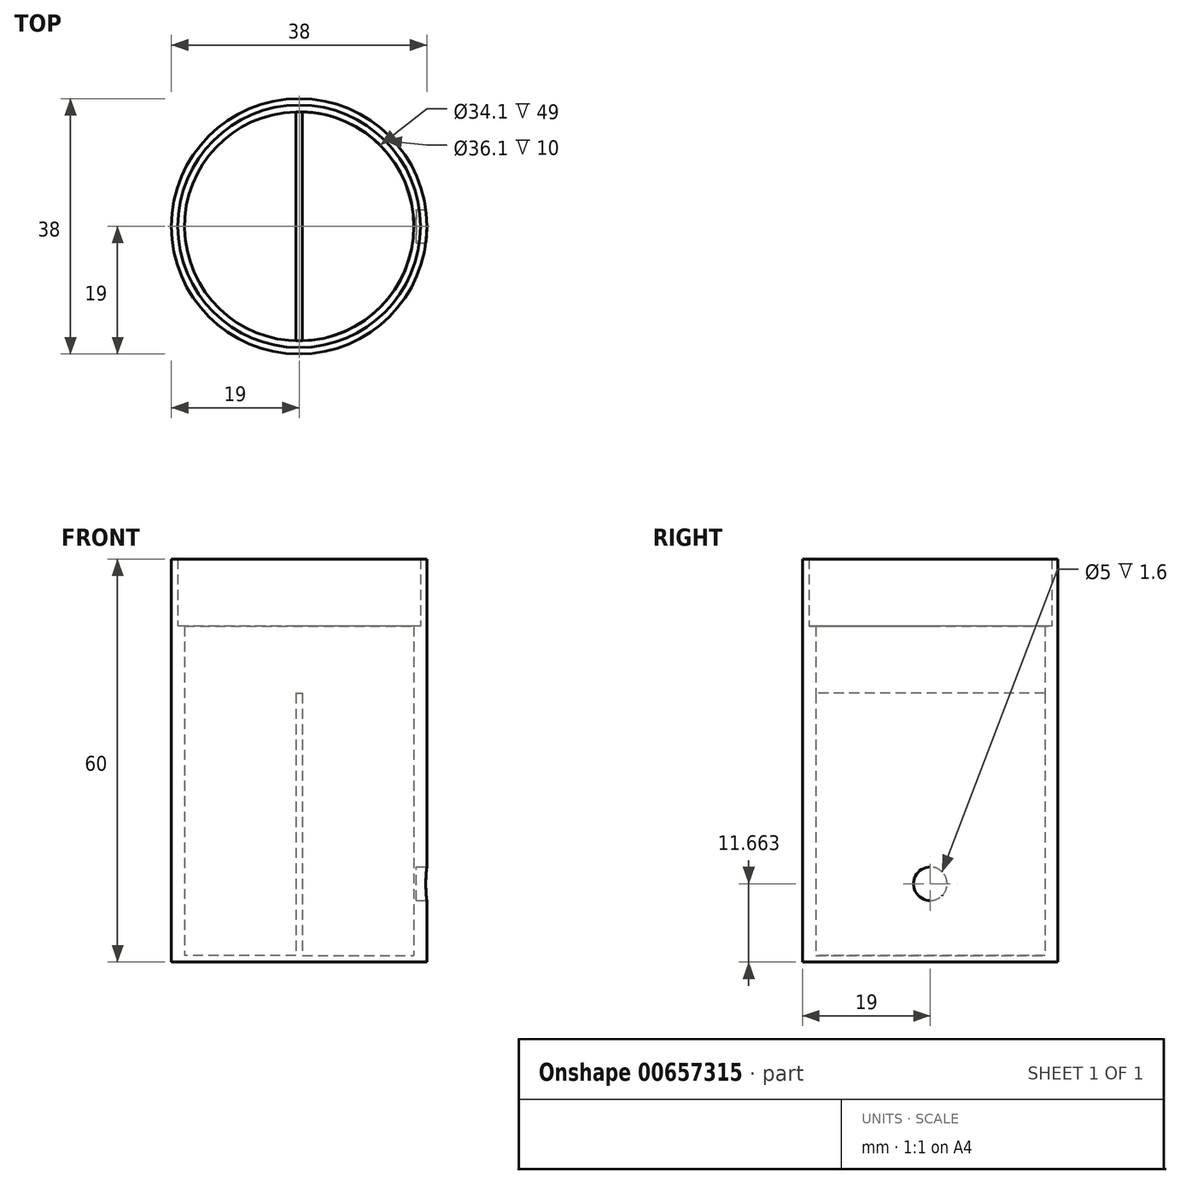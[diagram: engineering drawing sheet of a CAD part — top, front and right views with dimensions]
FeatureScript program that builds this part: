
annotation { "Feature Type Name" : "Feature", "Feature Type Description" : "" }
export const myFeature = defineFeature(function(context is Context, id is Id, definition is map)
    precondition{}
    {
        {
            var Q0;
            Q0=qCreatedBy(makeId("Top.planeOp"),FACE);
            var sketch = newSketch(context, id + "F0", { "sketchPlane" : qUnion([Q0])});
            skCircle(sketch, "E0", {"center": v(0, 0) * mm, "radius": 18.05 * mm});
            skCircle(sketch, "E1", {"center": v(0, 0) * mm, "radius": 17.05 * mm});
            skCircle(sketch, "E2", {"center": v(0, 0) * mm, "radius": 19 * mm});
            skLineSegment(sketch, "E3.bottom", {"start": v(0.5, 17.04) * mm, "end": v(-0.5, 17.04) * mm});
            skLineSegment(sketch, "E3.top", {"start": v(0.5, -17.04) * mm, "end": v(-0.5, -17.04) * mm});
            skLineSegment(sketch, "E3.left", {"start": v(0.5, 17.04) * mm, "end": v(0.5, -17.04) * mm});
            skLineSegment(sketch, "E3.right", {"start": v(-0.5, 17.04) * mm, "end": v(-0.5, -17.04) * mm});
            skSolve(sketch);
        }
        {
            var Q0;
            {var subQ0=sQuery(id+"F0.wireOp",EDGE,"E3.right");Q0=makeQuery(id+"F0.imprint","IMPRINT",FACE,{"disambiguationData":[TD([[makeQuery(id+"F0.imprint","IMPRINT",EDGE,{"derivedFrom":subQ0}),-1.0]])]});}
            var Q1;
            {var subQ0=sQuery(id+"F0.wireOp",EDGE,"E3.left");Q1=makeQuery(id+"F0.imprint","IMPRINT",FACE,{"disambiguationData":[TD([[makeQuery(id+"F0.imprint","IMPRINT",EDGE,{"derivedFrom":subQ0}),1.0]])]});}
            extrude(context, id + "F1", {"entities" : qUnion([Q0, Q1]), "depth" : 1 * mm, "offsetDistance" : 25 * mm});
        }
        {
            var Q0;
            Q0=makeQuery(id+"F0.imprint","IMPRINT",FACE,{"disambiguationData":[TD([[makeQuery(id+"F0.imprint","IMPRINT",EDGE,{"derivedFrom":sQuery(id+"F0.wireOp",EDGE,"E0")}),1.0]])]});
            extrude(context, id + "F2", {"entities" : qUnion([Q0]), "depth" : 50 * mm, "offsetDistance" : 25 * mm});
        }
        {
            var Q0;
            Q0=makeQuery(id+"F0.imprint","IMPRINT",FACE,{"disambiguationData":[TD([[makeQuery(id+"F0.imprint","IMPRINT",EDGE,{"derivedFrom":sQuery(id+"F0.wireOp",EDGE,"E3.bottom")}),1.0]])]});
            extrude(context, id + "F3", {"entities" : qUnion([Q0]), "operationType" : NewBodyOperationType.ADD, "depth" : 40 * mm, "offsetDistance" : 25 * mm});
        }
        {
            var Q0;
            Q0=makeQuery(id+"F0.imprint","IMPRINT",FACE,{"disambiguationData":[TD([[makeQuery(id+"F0.imprint","IMPRINT",EDGE,{"derivedFrom":sQuery(id+"F0.wireOp",EDGE,"E0")}),-1.0]])]});
            extrude(context, id + "F4", {"entities" : qUnion([Q0]), "operationType" : NewBodyOperationType.ADD, "depth" : 60 * mm, "offsetDistance" : 25 * mm});
        }
        {
            var Q0;
            Q0=qCreatedBy(makeId("Right.planeOp"),FACE);
            cPlane(context, id + "F5", {"entities" : qUnion([Q0]), "cplaneType" : CPlaneType.OFFSET, "offset" : 20.4 * mm, "width" : 150 * mm, "height" : 150 * mm});
        }
        {
            var Q0;
            Q0=qCreatedBy(id+"F5.planeOp",FACE);
            var sketch = newSketch(context, id + "F6", { "sketchPlane" : qUnion([Q0])});
            skCircle(sketch, "E4", {"center": v(0, 11.66) * mm, "radius": 2.5 * mm});
            skSolve(sketch);
        }
        {
            var Q0;
            Q0=makeQuery(id+"F6.imprint","IMPRINT",FACE,{"disambiguationData":[TD([[makeQuery(id+"F6.imprint","IMPRINT",EDGE,{"derivedFrom":sQuery(id+"F6.wireOp",EDGE,"E4")}),1.0]])]});
            extrude(context, id + "F7", {"entities" : qUnion([Q0]), "operationType" : NewBodyOperationType.REMOVE, "oppositeDirection" : true, "depth" : 3 * mm, "offsetDistance" : 25 * mm});
        }
    });
